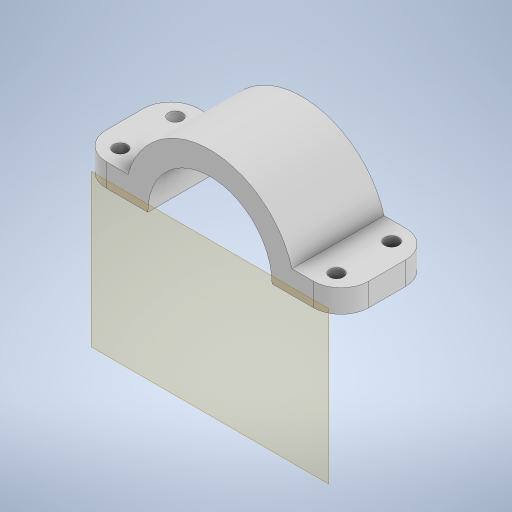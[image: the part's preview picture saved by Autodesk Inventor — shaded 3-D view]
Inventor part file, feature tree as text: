
AUTODESK INVENTOR PART (.ipt)
format: ipt  version: 2024.1 (Build 281209000, 209)  size: 290,304 bytes
history: native  units: mm
features: other x5, extrude x2, sketch x2, fillet x1
ambient origin geometry x8: Origin, YZ Plane, XZ Plane, XY Plane, X Axis, Y Axis, Z Axis, Center Point
bodies: Body1 (feature_tree)
feature tree (10):
  other  "Sólido1"
  other  "Plano de trabalho1"
  extrude  "Extrusão1"  Depth=13.5mm
  fillet  "Arredondamento1"  Radius=5.0mm
  extrude  "Extrusão2"  Depth=5.0mm
  sketch  "Esboço1"  dims[d0=27.0mm d1=13.5mm d2=5.0mm]
  sketch  "Esboço2"  dims[d3=10.0mm d4=5.0mm d5=10.0mm d6=5.0mm d7=5.0mm d8=5.0mm d9=20.0mm d10=0.0mm d11=6.0mm d12=20.0mm d13=0.0mm]
  other  "<userpath>\OneDrive\Área de Trabalho\Montagem2.iam"
  other  "Montagem2.iam"
  other  "Peça51:1"
